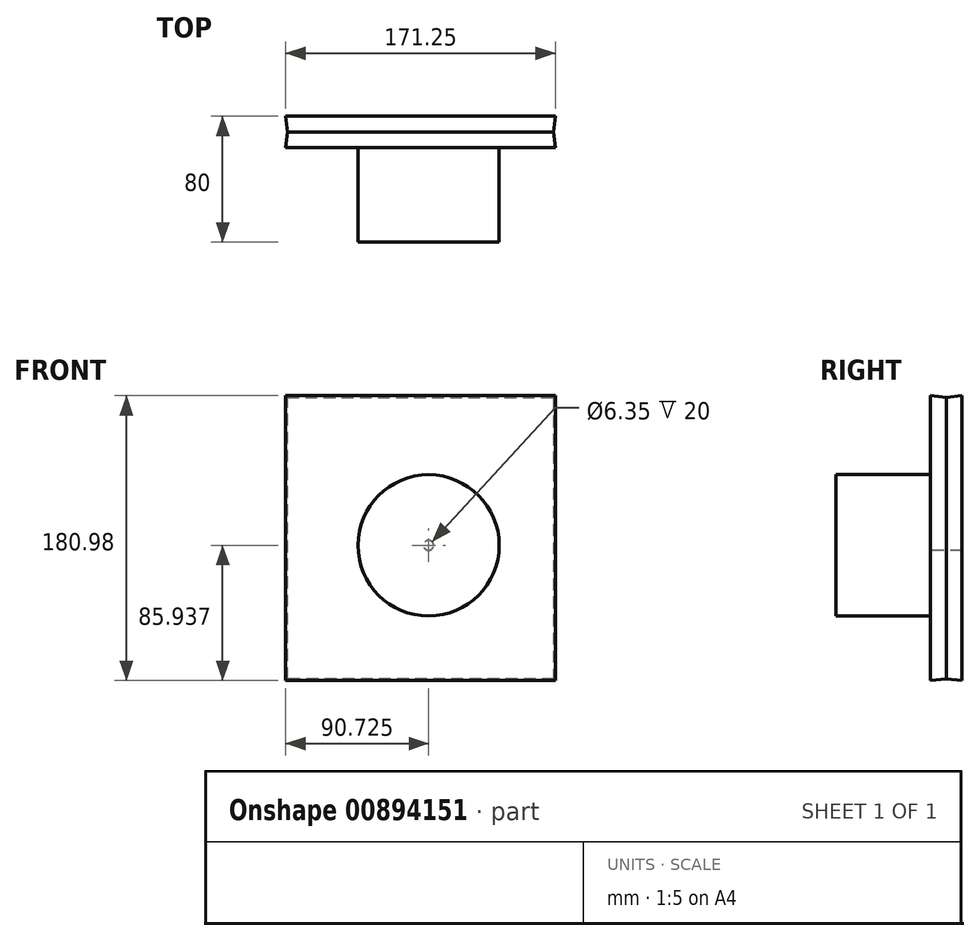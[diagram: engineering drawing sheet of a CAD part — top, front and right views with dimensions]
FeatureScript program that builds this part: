
annotation { "Feature Type Name" : "Feature", "Feature Type Description" : "" }
export const myFeature = defineFeature(function(context is Context, id is Id, definition is map)
    precondition{}
    {
        {
            var Q0;
            Q0=qCreatedBy(makeId("Front.planeOp"),FACE);
            var sketch = newSketch(context, id + "F0", { "sketchPlane" : qUnion([Q0])});
            skLineSegment(sketch, "E0.bottom", {"start": v(-41.19, -18.45) * mm, "end": v(127.96, -18.45) * mm});
            skLineSegment(sketch, "E0.top", {"start": v(-41.19, 160.43) * mm, "end": v(127.96, 160.43) * mm});
            skLineSegment(sketch, "E0.left", {"start": v(-41.19, -18.45) * mm, "end": v(-41.19, 160.43) * mm});
            skLineSegment(sketch, "E0.right", {"start": v(127.96, -18.45) * mm, "end": v(127.96, 160.43) * mm});
            skPoint(sketch, "E0.middle", {"position": v(43.38, 71) * mm});
            skSolve(sketch);
        }
        {
            var Q0;
            Q0 = qSketchRegion(id + "F0", true);
            var Q1;
            Q1=makeQuery(id+"F0.imprint","IMPRINT",FACE,{"disambiguationData":[TD([[makeQuery(id+"F0.imprint","IMPRINT",EDGE,{"derivedFrom":sQuery(id+"F0.wireOp",EDGE,"E0.bottom")}),1.0]])]});
            extrude(context, id + "F1", {"entities" : qUnion([Q0, Q1]), "endBound" : BoundingType.SYMMETRIC, "depth" : 20 * mm, "offsetDistance" : 25.4 * mm, "hasDraft" : true, "draftAngle" : 6 * degree});
        }
        {
            var Q0;
            Q0=makeQuery(id+"F1.opExtrude","CAP_FACE",FACE,{"disambiguationData":[OSD([sQuery(id+"F0.wireOp",EDGE,"E0.bottom"),sQuery(id+"F0.wireOp",EDGE,"E0.top"),sQuery(id+"F0.wireOp",EDGE,"E0.left"),sQuery(id+"F0.wireOp",EDGE,"E0.right")])],"isStart":false});
            var sketch = newSketch(context, id + "F2", { "sketchPlane" : qUnion([Q0])});
            skCircle(sketch, "E1", {"center": v(48.48, 66.44) * mm, "radius": 46.79 * mm});
            skSolve(sketch);
        }
        {
            var Q0;
            Q0=sQuery(id+"F2.wireOp",VERTEX,"E1.center");
            var Q1;
            Q1=makeQuery(id+"F1.*.split.splitOp","SPLIT",BODY,{"derivedFrom":makeQuery(id+"F1.opExtrude","SWEPT_BODY",BODY,{"disambiguationData":[OSD([sQuery(id+"F0.wireOp",EDGE,"E0.bottom"),sQuery(id+"F0.wireOp",EDGE,"E0.top"),sQuery(id+"F0.wireOp",EDGE,"E0.left"),sQuery(id+"F0.wireOp",EDGE,"E0.right")])]})});
            hole(context, id + "F3", {"style" : HoleStyle.SIMPLE, "endStyle" : HoleEndStyle.THROUGH, "holeDiameter" : 6.35 * mm, "majorDiameter" : 6.35 * mm, "isTappedThrough" : true, "tappedDepth" : 12.7 * mm, "tapClearance" : 3, "locations" : qUnion([Q0]), "scope" : qUnion([Q1])});
        }
        {
            var Q0;
            Q0=makeQuery(id+"F1.opExtrude","CAP_FACE",FACE,{"disambiguationData":[OSD([sQuery(id+"F0.wireOp",EDGE,"E0.bottom"),sQuery(id+"F0.wireOp",EDGE,"E0.top"),sQuery(id+"F0.wireOp",EDGE,"E0.left"),sQuery(id+"F0.wireOp",EDGE,"E0.right")])],"isStart":false});
            var sketch = newSketch(context, id + "F4", { "sketchPlane" : qUnion([Q0])});
            skCircle(sketch, "E2", {"center": v(48.48, 66.44) * mm, "radius": 44.87 * mm});
            skSolve(sketch);
        }
        {
            var Q0;
            Q0 = qSketchRegion(id + "F4", true);
            extrude(context, id + "F5", {"entities" : qUnion([Q0]), "operationType" : NewBodyOperationType.ADD, "depth" : 60 * mm, "offsetDistance" : 25.4 * mm});
        }
    });
